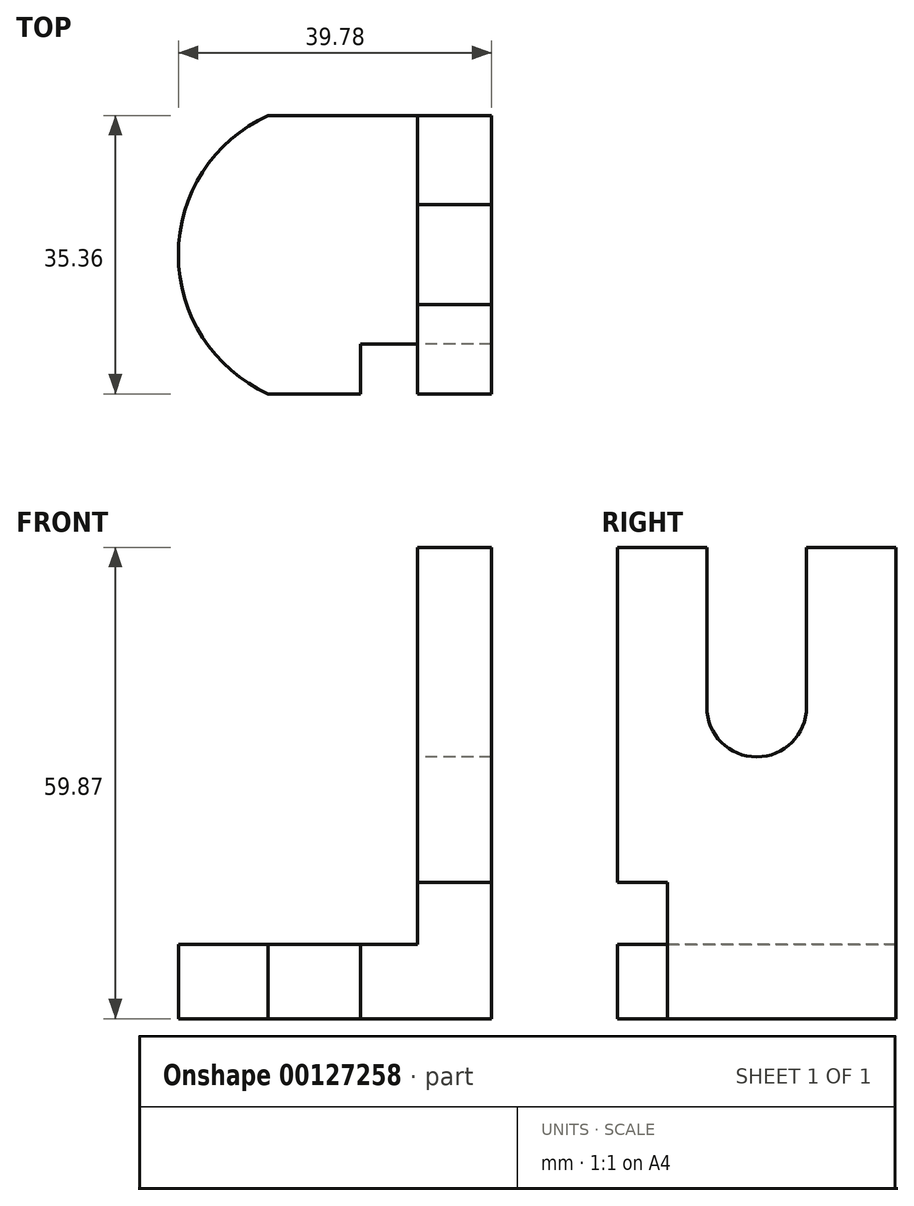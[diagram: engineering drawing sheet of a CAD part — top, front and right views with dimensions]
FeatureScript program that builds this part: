
annotation { "Feature Type Name" : "Feature", "Feature Type Description" : "" }
export const myFeature = defineFeature(function(context is Context, id is Id, definition is map)
    precondition{}
    {
        {
            var Q0;
            Q0=qCreatedBy(makeId("Front.planeOp"),FACE);
            var sketch = newSketch(context, id + "F0", { "sketchPlane" : qUnion([Q0])});
            skLineSegment(sketch, "E0", {"start": v(0, 59.87) * mm, "end": v(0, 0) * mm});
            skLineSegment(sketch, "E1", {"start": v(0, 0) * mm, "end": v(-42.38, 0) * mm});
            skLineSegment(sketch, "E2", {"start": v(-42.38, 0) * mm, "end": v(-42.38, 9.4) * mm});
            skLineSegment(sketch, "E3", {"start": v(-42.38, 9.4) * mm, "end": v(-9.4, 9.4) * mm});
            skLineSegment(sketch, "E4", {"start": v(-9.4, 9.4) * mm, "end": v(-9.4, 59.87) * mm});
            skLineSegment(sketch, "E5", {"start": v(-9.4, 59.87) * mm, "end": v(0, 59.87) * mm});
            skSolve(sketch);
        }
        {
            var Q0;
            Q0=makeQuery(id+"F0.imprint","IMPRINT",FACE,{"disambiguationData":[TD([[makeQuery(id+"F0.imprint","IMPRINT",EDGE,{"derivedFrom":sQuery(id+"F0.wireOp",EDGE,"E0")}),-1.0]])]});
            extrude(context, id + "F1", {"entities" : qUnion([Q0]), "depth" : 35.35 * mm, "symmetric" : true});
        }
        {
            var Q0;
            Q0=makeQuery(id+"F1.opExtrude","SWEPT_FACE",FACE,{"disambiguationData":[OSD([sQuery(id+"F0.wireOp",EDGE,"E4")])]});
            var sketch = newSketch(context, id + "F2", { "sketchPlane" : qUnion([Q0])});
            skLineSegment(sketch, "E6.bottom", {"start": v(-6.34, 59.87) * mm, "end": v(6.34, 59.87) * mm});
            skLineSegment(sketch, "E6.left", {"start": v(-6.34, 59.87) * mm, "end": v(-6.34, 39.59) * mm});
            skLineSegment(sketch, "E6.right", {"start": v(6.34, 59.87) * mm, "end": v(6.34, 39.59) * mm});
            skArc(sketch, "E7", {"start": v(-6.34, 39.59) * mm, "mid": v(0, 33.25) * mm, "end": v(6.34, 39.59) * mm});
            skLineSegment(sketch, "E8", {"start": v(0, 0) * mm, "end": v(0, 39.59) * mm, "construction": true});
            skSolve(sketch);
        }
        {
            var Q0;
            Q0 = qSketchRegion(id + "F2", true);
            extrude(context, id + "F3", {"entities" : qUnion([Q0]), "operationType" : NewBodyOperationType.REMOVE, "endBound" : BoundingType.THROUGH_ALL, "oppositeDirection" : true, "depth" : 25.4 * mm});
        }
        {
            var Q0;
            Q0=makeQuery(id+"F1.opExtrude","SWEPT_FACE",FACE,{"disambiguationData":[OSD([sQuery(id+"F0.wireOp",EDGE,"E3")])]});
            var sketch = newSketch(context, id + "F4", { "sketchPlane" : qUnion([Q0])});
            skArc(sketch, "E9", {"start": v(-28.41, 17.68) * mm, "mid": v(-39.78, 0) * mm, "end": v(-28.41, -17.68) * mm});
            skLineSegment(sketch, "E10", {"start": v(-28.41, 17.68) * mm, "end": v(-42.38, 17.68) * mm});
            skLineSegment(sketch, "E11", {"start": v(-42.38, 17.68) * mm, "end": v(-42.38, -17.68) * mm});
            skLineSegment(sketch, "E12", {"start": v(-42.38, -17.68) * mm, "end": v(-28.41, -17.68) * mm});
            skSolve(sketch);
        }
        {
            var Q0;
            Q0 = qSketchRegion(id + "F4", true);
            extrude(context, id + "F5", {"entities" : qUnion([Q0]), "operationType" : NewBodyOperationType.REMOVE, "endBound" : BoundingType.THROUGH_ALL, "oppositeDirection" : true, "depth" : 25.4 * mm});
        }
        {
            var Q0;
            Q0=makeQuery(id+"F1.opExtrude","CAP_FACE",FACE,{"disambiguationData":[OSD([sQuery(id+"F0.wireOp",EDGE,"E0"),sQuery(id+"F0.wireOp",EDGE,"E1"),sQuery(id+"F0.wireOp",EDGE,"E2"),sQuery(id+"F0.wireOp",EDGE,"E3"),sQuery(id+"F0.wireOp",EDGE,"E4"),sQuery(id+"F0.wireOp",EDGE,"E5")])],"isStart":false});
            var sketch = newSketch(context, id + "F6", { "sketchPlane" : qUnion([Q0])});
            skLineSegment(sketch, "E13.bottom", {"start": v(0, 0) * mm, "end": v(-16.62, 0) * mm});
            skLineSegment(sketch, "E13.top", {"start": v(0, 17.34) * mm, "end": v(-16.62, 17.34) * mm});
            skLineSegment(sketch, "E13.left", {"start": v(0, 0) * mm, "end": v(0, 17.34) * mm});
            skLineSegment(sketch, "E13.right", {"start": v(-16.62, 0) * mm, "end": v(-16.62, 17.34) * mm});
            skSolve(sketch);
        }
        {
            var Q0;
            Q0 = qSketchRegion(id + "F6", true);
            extrude(context, id + "F7", {"entities" : qUnion([Q0]), "operationType" : NewBodyOperationType.REMOVE, "oppositeDirection" : true, "depth" : 6.35 * mm});
        }
    });
